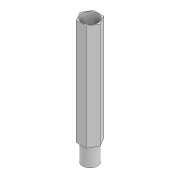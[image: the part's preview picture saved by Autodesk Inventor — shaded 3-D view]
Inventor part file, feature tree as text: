
AUTODESK INVENTOR PART (.ipt)
format: ipt  version: 2021 (Build 250183000, 183)  size: 91,648 bytes
history: native  units: mm
features: sketch x3, extrude x2, other x1, hole x1
ambient origin geometry x8: Origin, YZ Plane, XZ Plane, XY Plane, X Axis, Y Axis, Z Axis, Center Point
bodies: Body1 (feature_tree)
feature tree (7):
  other  "Твердое тело1"
  extrude  "Выдавливание1"  Depth=2.8mm
  hole  "Отверстие1"  [1 undecoded]
  extrude  "Выдавливание2"  Depth=2.4mm
  sketch  "Эскиз1"
  sketch  "Эскиз2"
  sketch  "Эскиз3"
note: 1 required parameter value undecoded (feature->parameter linkage not recoverable at this tier; creation-order binding heuristic only, values carry confidence <= 0.55)
